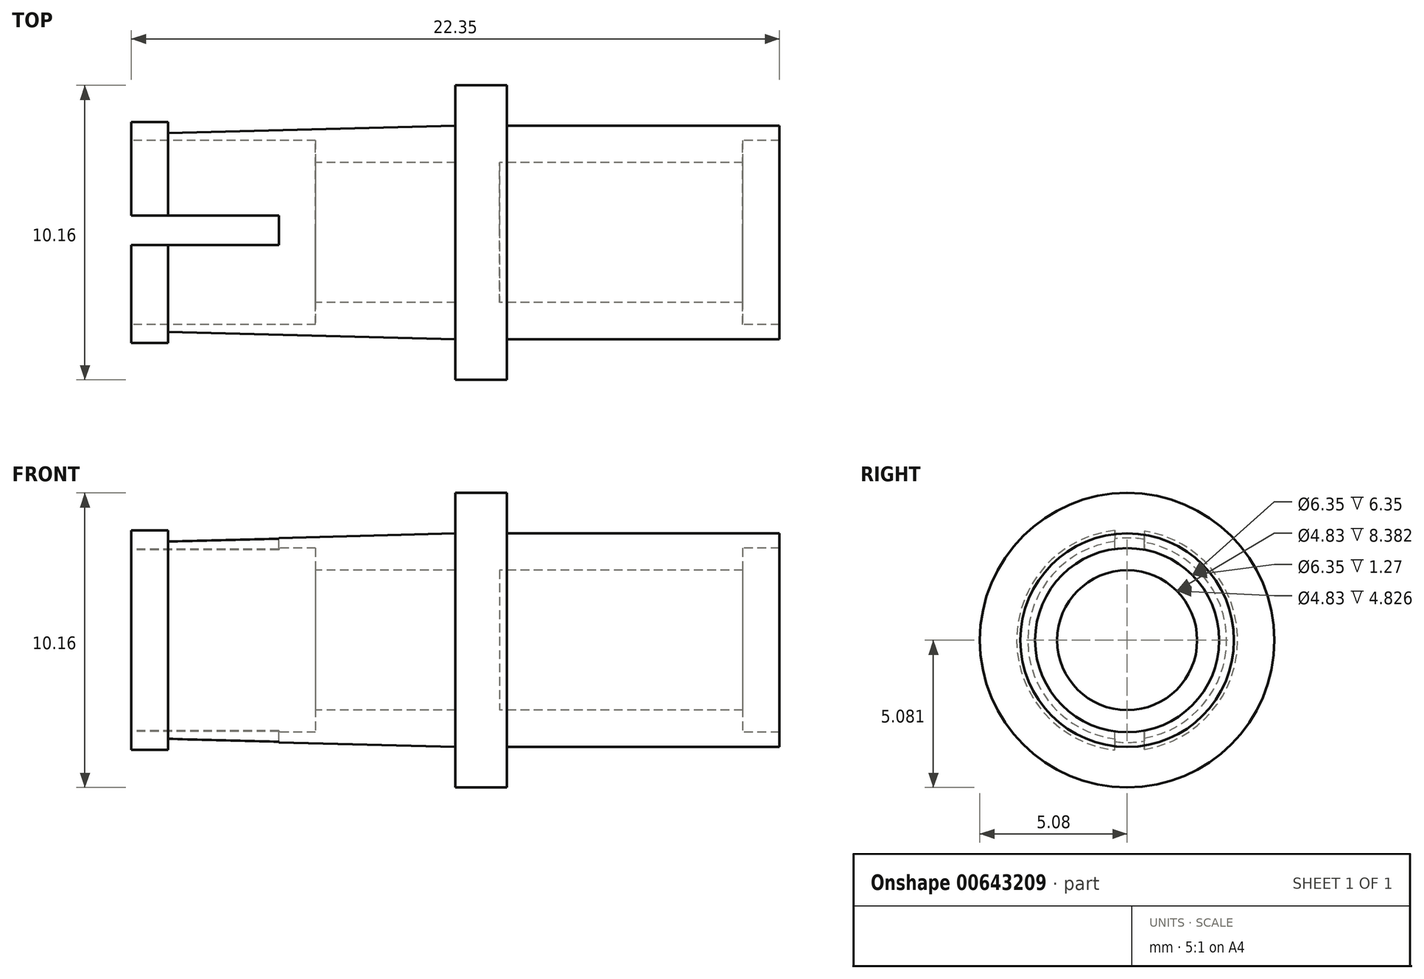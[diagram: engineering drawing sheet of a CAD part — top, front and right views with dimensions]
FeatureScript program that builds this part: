
annotation { "Feature Type Name" : "Feature", "Feature Type Description" : "" }
export const myFeature = defineFeature(function(context is Context, id is Id, definition is map)
    precondition{}
    {
        {
            var Q0;
            Q0=qCreatedBy(makeId("Front.planeOp"),FACE);
            var sketch = newSketch(context, id + "F0", { "sketchPlane" : qUnion([Q0])});
            skLineSegment(sketch, "E0", {"start": v(-10.17, -9.6) * mm, "end": v(-8.65, -9.6) * mm});
            skLineSegment(sketch, "E1", {"start": v(-8.65, -9.6) * mm, "end": v(-8.65, -7.2) * mm});
            skLineSegment(sketch, "E2", {"start": v(-8.65, -7.2) * mm, "end": v(-0.27, -7.2) * mm});
            skLineSegment(sketch, "E3", {"start": v(-0.27, -7.2) * mm, "end": v(-0.27, -6.43) * mm});
            skLineSegment(sketch, "E4", {"start": v(-0.27, -6.43) * mm, "end": v(1, -6.43) * mm});
            skLineSegment(sketch, "E5", {"start": v(1, -6.43) * mm, "end": v(1, -5.93) * mm});
            skLineSegment(sketch, "E6", {"start": v(1, -5.93) * mm, "end": v(-8.4, -5.93) * mm});
            skLineSegment(sketch, "E7", {"start": v(-8.4, -5.93) * mm, "end": v(-8.4, -4.53) * mm});
            skLineSegment(sketch, "E8", {"start": v(-8.4, -4.53) * mm, "end": v(-10.17, -4.53) * mm});
            skLineSegment(sketch, "E9", {"start": v(-10.17, -4.53) * mm, "end": v(-10.17, -5.93) * mm});
            skLineSegment(sketch, "E10", {"start": v(-10.17, -5.93) * mm, "end": v(-20.08, -6.18) * mm});
            skLineSegment(sketch, "E11", {"start": v(-20.08, -6.18) * mm, "end": v(-20.08, -5.8) * mm});
            skLineSegment(sketch, "E12", {"start": v(-20.08, -5.8) * mm, "end": v(-21.35, -5.8) * mm});
            skLineSegment(sketch, "E13", {"start": v(-21.35, -5.8) * mm, "end": v(-21.35, -6.43) * mm});
            skLineSegment(sketch, "E14", {"start": v(-21.35, -6.43) * mm, "end": v(-15, -6.43) * mm});
            skLineSegment(sketch, "E15", {"start": v(-15, -6.43) * mm, "end": v(-15, -7.2) * mm});
            skLineSegment(sketch, "E16", {"start": v(-15, -7.2) * mm, "end": v(-10.17, -7.2) * mm});
            skLineSegment(sketch, "E17", {"start": v(-10.17, -7.2) * mm, "end": v(-10.17, -9.6) * mm});
            skLineSegment(sketch, "E18", {"start": v(-16.9, -9.6) * mm, "end": v(5.35, -9.6) * mm, "construction": true});
            skLineSegment(sketch, "E19.MirrorCS", {"start": v(1, -12.78) * mm, "end": v(1, -13.3) * mm});
            skLineSegment(sketch, "E20.MirrorCS", {"start": v(-20.08, -13.04) * mm, "end": v(-20.08, -13.42) * mm});
            skLineSegment(sketch, "E21.MirrorCS", {"start": v(-0.27, -12.02) * mm, "end": v(-0.27, -12.78) * mm});
            skLineSegment(sketch, "E22.MirrorCS", {"start": v(-15, -12.02) * mm, "end": v(-10.17, -12.02) * mm});
            skLineSegment(sketch, "E23.MirrorCS", {"start": v(-10.17, -13.3) * mm, "end": v(-20.08, -13.04) * mm});
            skLineSegment(sketch, "E24.MirrorCS", {"start": v(-8.4, -13.3) * mm, "end": v(-8.4, -14.69) * mm});
            skLineSegment(sketch, "E25.MirrorCS", {"start": v(-15, -12.78) * mm, "end": v(-15, -12.02) * mm});
            skLineSegment(sketch, "E26.MirrorCS", {"start": v(-8.65, -9.6) * mm, "end": v(-8.65, -12.02) * mm});
            skLineSegment(sketch, "E27.MirrorCS", {"start": v(1, -13.3) * mm, "end": v(-8.4, -13.3) * mm});
            skLineSegment(sketch, "E28.MirrorCS", {"start": v(-8.65, -12.02) * mm, "end": v(-0.27, -12.02) * mm});
            skLineSegment(sketch, "E29.MirrorCS", {"start": v(-0.27, -12.78) * mm, "end": v(1, -12.78) * mm});
            skLineSegment(sketch, "E30.MirrorCS", {"start": v(-10.17, -14.69) * mm, "end": v(-10.17, -13.3) * mm});
            skLineSegment(sketch, "E31.MirrorCS", {"start": v(-10.17, -12.02) * mm, "end": v(-10.17, -9.6) * mm});
            skLineSegment(sketch, "E32.MirrorCS", {"start": v(-21.35, -12.78) * mm, "end": v(-15, -12.78) * mm});
            skLineSegment(sketch, "E33.MirrorCS", {"start": v(-21.35, -13.42) * mm, "end": v(-21.35, -12.78) * mm});
            skLineSegment(sketch, "E34.MirrorCS", {"start": v(-20.08, -13.42) * mm, "end": v(-21.35, -13.42) * mm});
            skLineSegment(sketch, "E35.MirrorCS", {"start": v(-8.4, -14.69) * mm, "end": v(-10.17, -14.69) * mm});
            skSolve(sketch);
        }
        {
            var Q0;
            Q0=makeQuery(id+"F0.imprint","IMPRINT",FACE,{"disambiguationData":[TD([[makeQuery(id+"F0.imprint","IMPRINT",EDGE,{"derivedFrom":sQuery(id+"F0.wireOp",EDGE,"E1")}),1.0]])]});
            var Q1;
            Q1=sQuery(id+"F0.wireOp",EDGE,"E18");
            revolve(context, id + "F1", {"entities" : qUnion([Q0]), "axis" : qUnion([Q1]), "revolveType" : RevolveType.FULL});
        }
        {
            var Q0;
            Q0=qCreatedBy(makeId("Top.planeOp"),FACE);
            var sketch = newSketch(context, id + "F2", { "sketchPlane" : qUnion([Q0])});
            skLineSegment(sketch, "E36", {"start": v(-21.35, 0.59) * mm, "end": v(-16.27, 0.59) * mm});
            skLineSegment(sketch, "E37", {"start": v(-16.27, 0.59) * mm, "end": v(-16.27, -0.43) * mm});
            skLineSegment(sketch, "E38", {"start": v(-16.27, -0.43) * mm, "end": v(-21.35, -0.43) * mm});
            skLineSegment(sketch, "E39", {"start": v(-21.35, -0.43) * mm, "end": v(-21.35, 0.59) * mm});
            skSolve(sketch);
        }
        {
            var Q0;
            Q0 = qSketchRegion(id + "F2", true);
            extrude(context, id + "F3", {"entities" : qUnion([Q0]), "operationType" : NewBodyOperationType.REMOVE, "oppositeDirection" : true, "depth" : 25.4 * mm, "offsetDistance" : 25.4 * mm});
        }
    });
